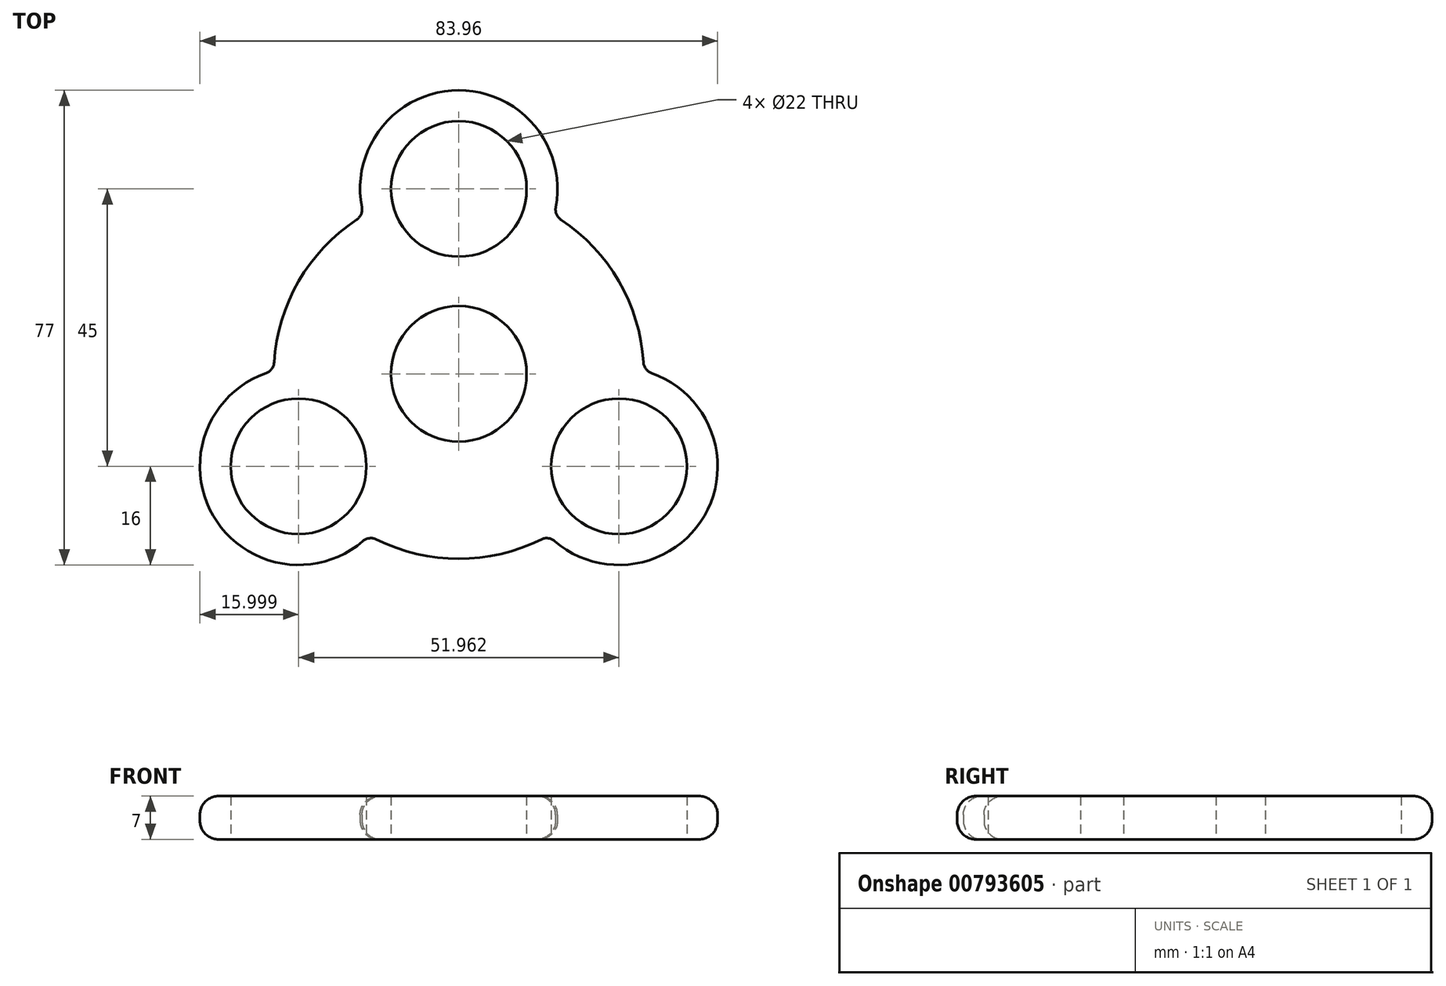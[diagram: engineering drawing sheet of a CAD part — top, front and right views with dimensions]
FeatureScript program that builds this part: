
annotation { "Feature Type Name" : "Feature", "Feature Type Description" : "" }
export const myFeature = defineFeature(function(context is Context, id is Id, definition is map)
    precondition{}
    {
        {
            var Q0;
            Q0=qCreatedBy(makeId("Top.planeOp"),FACE);
            var sketch = newSketch(context, id + "F0", { "sketchPlane" : qUnion([Q0])});
            skCircle(sketch, "E0", {"center": v(0, 0) * mm, "radius": 11 * mm});
            skArc(sketch, "E1", {"start": v(-16.58, 25) * mm, "mid": v(-25.98, 15) * mm, "end": v(-29.94, 1.86) * mm});
            skCircle(sketch, "E2", {"center": v(25.98, -15) * mm, "radius": 11 * mm});
            skCircle(sketch, "E3", {"center": v(0, 30) * mm, "radius": 11 * mm});
            skCircle(sketch, "E4", {"center": v(-25.98, -15) * mm, "radius": 11 * mm});
            skLineSegment(sketch, "E5", {"start": v(0, 30) * mm, "end": v(0, 0) * mm, "construction": true});
            skLineSegment(sketch, "E6", {"start": v(25.98, -15) * mm, "end": v(0, 0) * mm, "construction": true});
            skLineSegment(sketch, "E7", {"start": v(-16.45, -9.5) * mm, "end": v(0, 0) * mm, "construction": true});
            skArc(sketch, "E8.0", {"start": v(15.55, -27.14) * mm, "mid": v(39.84, -23) * mm, "end": v(31.28, 0.1) * mm});
            skArc(sketch, "E9.0", {"start": v(-31.28, 0.1) * mm, "mid": v(-39.84, -23) * mm, "end": v(-15.55, -27.14) * mm});
            skArc(sketch, "E10.0", {"start": v(15.72, 27.04) * mm, "mid": v(0, 46) * mm, "end": v(-15.72, 27.04) * mm});
            skArc(sketch, "E11.trimOffspring", {"start": v(29.94, 1.86) * mm, "mid": v(25.98, 15) * mm, "end": v(16.58, 25) * mm});
            skArc(sketch, "E12.trimOffspring", {"start": v(-13.36, -26.86) * mm, "mid": v(0, -30) * mm, "end": v(13.36, -26.86) * mm});
            skPoint(sketch, "E13.visualSharp", {"position": v(-14.58, -26.22) * mm});
            skArc(sketch, "E13.filletArc", {"start": v(-13.36, -26.86) * mm, "mid": v(-14.5, -26.67) * mm, "end": v(-15.55, -27.14) * mm});
            skPoint(sketch, "E14.visualSharp", {"position": v(14.58, -26.22) * mm});
            skArc(sketch, "E14.filletArc", {"start": v(15.55, -27.14) * mm, "mid": v(14.5, -26.67) * mm, "end": v(13.36, -26.86) * mm});
            skPoint(sketch, "E15.visualSharp", {"position": v(30, 0.49) * mm});
            skArc(sketch, "E15.filletArc", {"start": v(29.94, 1.86) * mm, "mid": v(30.34, 0.78) * mm, "end": v(31.28, 0.1) * mm});
            skPoint(sketch, "E16.visualSharp", {"position": v(15.42, 25.73) * mm});
            skArc(sketch, "E16.filletArc", {"start": v(15.72, 27.04) * mm, "mid": v(15.85, 25.89) * mm, "end": v(16.58, 25) * mm});
            skPoint(sketch, "E17.visualSharp", {"position": v(-15.42, 25.73) * mm});
            skArc(sketch, "E17.filletArc", {"start": v(-16.58, 25) * mm, "mid": v(-15.85, 25.89) * mm, "end": v(-15.72, 27.04) * mm});
            skPoint(sketch, "E18.visualSharp", {"position": v(-30, 0.49) * mm});
            skArc(sketch, "E18.filletArc", {"start": v(-31.28, 0.1) * mm, "mid": v(-30.34, 0.78) * mm, "end": v(-29.94, 1.86) * mm});
            skSolve(sketch);
        }
        {
            var Q0;
            Q0=makeQuery(id+"F0.imprint","IMPRINT",FACE,{"disambiguationData":[TD([[makeQuery(id+"F0.imprint","IMPRINT",EDGE,{"derivedFrom":sQuery(id+"F0.wireOp",EDGE,"E0")}),-1.0]])]});
            extrude(context, id + "F1", {"entities" : qUnion([Q0]), "depth" : 7 * mm, "offsetDistance" : 25 * mm});
        }
        {
            var Q0;
            Q0=makeQuery(id+"F1.opExtrude","CAP_EDGE",EDGE,{"disambiguationData":[OSD([sQuery(id+"F0.wireOp",EDGE,"E12.trimOffspring")])],"isStart":false});
            var Q1;
            Q1=makeQuery(id+"F1.opExtrude","CAP_EDGE",EDGE,{"disambiguationData":[OSD([sQuery(id+"F0.wireOp",EDGE,"E12.trimOffspring")])],"isStart":true});
            fillet(context, id + "F2", {"entities" : qUnion([Q0, Q1]), "radius" : 3 * mm, "tangentPropagation" : true, "allowEdgeOverflow" : false});
        }
    });
